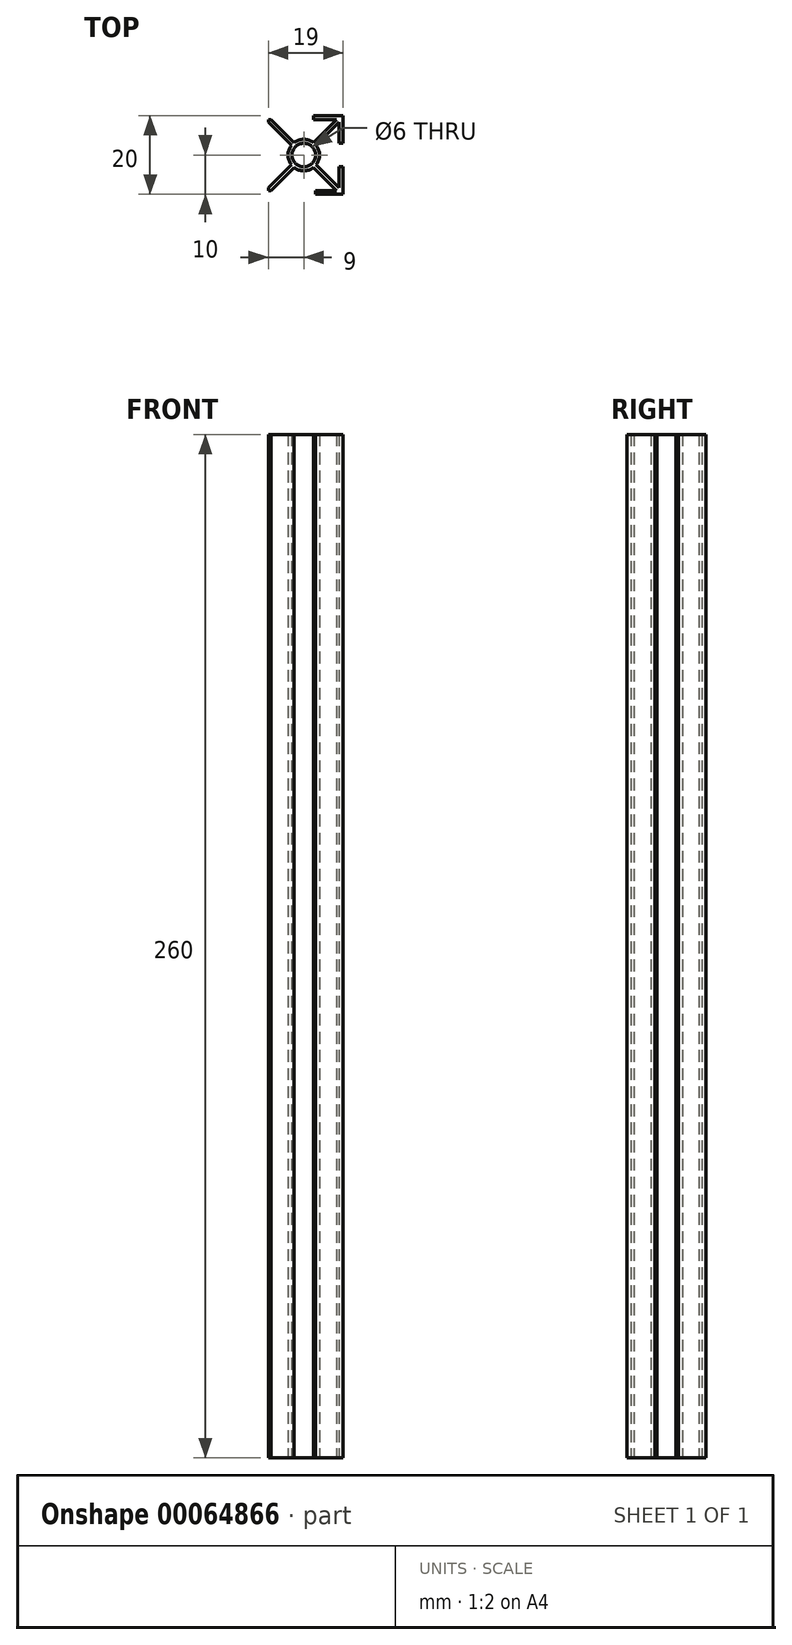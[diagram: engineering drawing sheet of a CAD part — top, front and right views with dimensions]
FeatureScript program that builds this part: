
annotation { "Feature Type Name" : "Feature", "Feature Type Description" : "" }
export const myFeature = defineFeature(function(context is Context, id is Id, definition is map)
    precondition{}
    {
        {
            var Q0;
            Q0=qCreatedBy(makeId("Top.planeOp"),FACE);
            var sketch = newSketch(context, id + "F0", { "sketchPlane" : qUnion([Q0])});
            skLineSegment(sketch, "E0.bottom", {"start": v(0, 0) * mm, "end": v(20, 0) * mm});
            skLineSegment(sketch, "E0.top", {"start": v(0, 20) * mm, "end": v(20, 20) * mm});
            skLineSegment(sketch, "E0.left", {"start": v(0, 0) * mm, "end": v(0, 20) * mm});
            skLineSegment(sketch, "E0.right", {"start": v(20, 0) * mm, "end": v(20, 20) * mm});
            skLineSegment(sketch, "E1", {"start": v(0, 20) * mm, "end": v(0, 13) * mm});
            skLineSegment(sketch, "E2.0", {"start": v(1, 19) * mm, "end": v(19, 19) * mm});
            skLineSegment(sketch, "E2.1", {"start": v(1, 1) * mm, "end": v(1, 19) * mm});
            skLineSegment(sketch, "E2.2", {"start": v(1, 1) * mm, "end": v(19, 1) * mm});
            skLineSegment(sketch, "E2.3", {"start": v(19, 1) * mm, "end": v(19, 19) * mm});
            skCircle(sketch, "E3", {"center": v(10, 10) * mm, "radius": 3 * mm});
            skPoint(sketch, "E3.centerSnap0", {"position": v(10, 0) * mm});
            skPoint(sketch, "E3.centerSnap1", {"position": v(0, 10) * mm});
            skCircle(sketch, "E4", {"center": v(10, 10) * mm, "radius": 4 * mm});
            skLineSegment(sketch, "E5", {"start": v(0, 13) * mm, "end": v(1, 13) * mm});
            skLineSegment(sketch, "E6", {"start": v(19, 13) * mm, "end": v(20, 13) * mm});
            skLineSegment(sketch, "E7", {"start": v(0, 0) * mm, "end": v(0, 7) * mm});
            skLineSegment(sketch, "E8", {"start": v(0, 7) * mm, "end": v(1, 7) * mm});
            skLineSegment(sketch, "E9", {"start": v(19, 7) * mm, "end": v(20, 7) * mm});
            skLineSegment(sketch, "E10", {"start": v(1, 18.3) * mm, "end": v(6.84, 12.45) * mm});
            skLineSegment(sketch, "E11", {"start": v(1.7, 19) * mm, "end": v(7.55, 13.16) * mm});
            skLineSegment(sketch, "E12", {"start": v(12.45, 13.16) * mm, "end": v(18.3, 19) * mm});
            skLineSegment(sketch, "E13", {"start": v(1, 1.7) * mm, "end": v(6.84, 7.55) * mm});
            skLineSegment(sketch, "E14", {"start": v(1.7, 1) * mm, "end": v(7.55, 6.84) * mm});
            skLineSegment(sketch, "E15", {"start": v(12.45, 6.84) * mm, "end": v(18.3, 1) * mm});
            skLineSegment(sketch, "E16", {"start": v(19, 1.7) * mm, "end": v(13.16, 7.55) * mm});
            skLineSegment(sketch, "E17", {"start": v(0, 0) * mm, "end": v(7, 0) * mm});
            skLineSegment(sketch, "E18", {"start": v(7, 1) * mm, "end": v(1.7, 1) * mm});
            skLineSegment(sketch, "E19", {"start": v(7, 19) * mm, "end": v(7, 20) * mm});
            skLineSegment(sketch, "E20", {"start": v(20, 0) * mm, "end": v(13, 0) * mm});
            skLineSegment(sketch, "E21", {"start": v(13, 0) * mm, "end": v(13, 1) * mm});
            skLineSegment(sketch, "E22", {"start": v(12.45, 19) * mm, "end": v(12.45, 20) * mm});
            skLineSegment(sketch, "E23", {"start": v(13.16, 12.45) * mm, "end": v(19, 18.3) * mm});
            skLineSegment(sketch, "E24", {"start": v(7, 0) * mm, "end": v(7, 1) * mm});
            skSolve(sketch);
        }
        {
            var Q0;
            {var subQ5=sQuery(id+"F0.wireOp",EDGE,"E1");Q0=makeQuery(id+"F0.imprint","IMPRINT",FACE,{"disambiguationData":[TD([[makeQuery(id+"F0.imprint","IMPRINT",EDGE,{"derivedFrom":subQ5}),1.0]])]});}
            var Q1;
            {var subQ0=sQuery(id+"F0.wireOp",EDGE,"E10");Q1=makeQuery(id+"F0.imprint","IMPRINT",FACE,{"disambiguationData":[TD([[makeQuery(id+"F0.imprint","IMPRINT",EDGE,{"derivedFrom":subQ0}),1.0]])]});}
            var Q2;
            {var subQ4=sQuery(id+"F0.wireOp",EDGE,"E6");Q2=makeQuery(id+"F0.imprint","IMPRINT",FACE,{"disambiguationData":[TD([[makeQuery(id+"F0.imprint","IMPRINT",EDGE,{"derivedFrom":subQ4}),1.0]])]});}
            var Q3;
            {var subQ0=sQuery(id+"F0.wireOp",EDGE,"E12");Q3=makeQuery(id+"F0.imprint","IMPRINT",FACE,{"disambiguationData":[TD([[makeQuery(id+"F0.imprint","IMPRINT",EDGE,{"derivedFrom":subQ0}),-1.0]])]});}
            var Q4;
            {var subQ8=sQuery(id+"F0.wireOp",EDGE,"E9");Q4=makeQuery(id+"F0.imprint","IMPRINT",FACE,{"disambiguationData":[TD([[makeQuery(id+"F0.imprint","IMPRINT",EDGE,{"derivedFrom":subQ8}),-1.0]])]});}
            var Q5;
            {var subQ0=sQuery(id+"F0.wireOp",EDGE,"E15");Q5=makeQuery(id+"F0.imprint","IMPRINT",FACE,{"disambiguationData":[TD([[makeQuery(id+"F0.imprint","IMPRINT",EDGE,{"derivedFrom":subQ0}),1.0]])]});}
            var Q6;
            Q6=makeQuery(id+"F0.imprint","IMPRINT",FACE,{"disambiguationData":[TD([[makeQuery(id+"F0.imprint","IMPRINT",EDGE,{"derivedFrom":sQuery(id+"F0.wireOp",EDGE,"E7")}),-1.0]])]});
            var Q7;
            {var subQ0=sQuery(id+"F0.wireOp",EDGE,"E13");Q7=makeQuery(id+"F0.imprint","IMPRINT",FACE,{"disambiguationData":[TD([[makeQuery(id+"F0.imprint","IMPRINT",EDGE,{"derivedFrom":subQ0}),-1.0]])]});}
            var Q8;
            Q8=makeQuery(id+"F0.imprint","IMPRINT",FACE,{"disambiguationData":[TD([[makeQuery(id+"F0.imprint","IMPRINT",EDGE,{"derivedFrom":sQuery(id+"F0.wireOp",EDGE,"E3")}),-1.0]])]});
            extrude(context, id + "F1", {"entities" : qUnion([Q0, Q1, Q2, Q3, Q4, Q5, Q6, Q7, Q8]), "depth" : 260 * mm});
        }
    });
